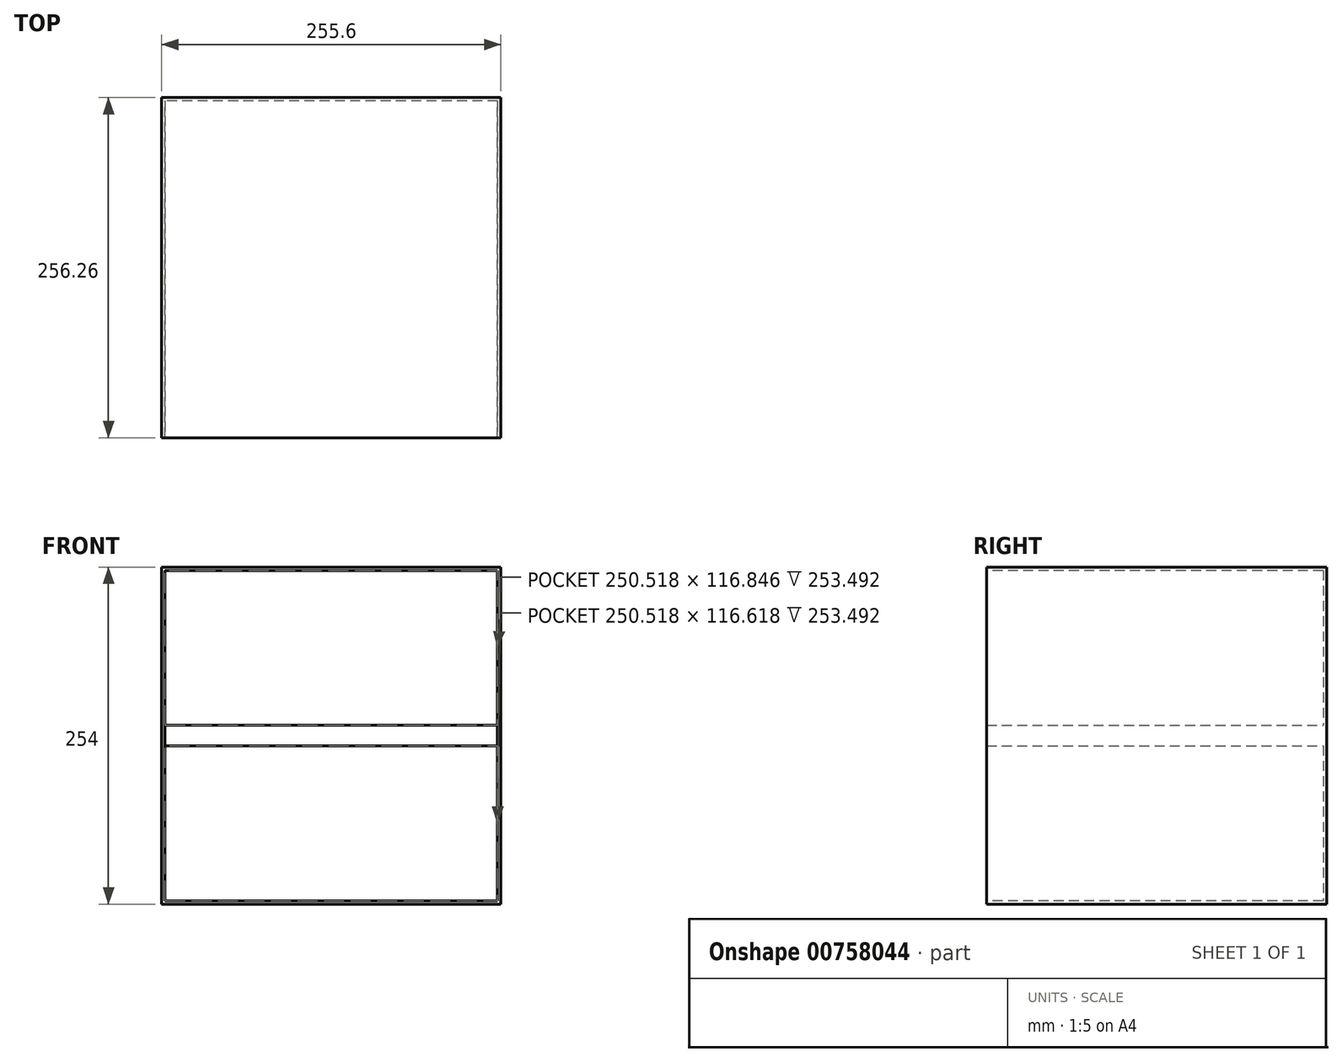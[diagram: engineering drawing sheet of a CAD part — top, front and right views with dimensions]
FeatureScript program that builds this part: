
annotation { "Feature Type Name" : "Feature", "Feature Type Description" : "" }
export const myFeature = defineFeature(function(context is Context, id is Id, definition is map)
    precondition{}
    {
        {
            var Q0;
            Q0=qCreatedBy(makeId("Top.planeOp"),FACE);
            var sketch = newSketch(context, id + "F0", { "sketchPlane" : qUnion([Q0])});
            skLineSegment(sketch, "E0.bottom", {"start": v(-150.52, 117.37) * mm, "end": v(105.08, 117.37) * mm});
            skLineSegment(sketch, "E0.top", {"start": v(-150.52, -138.89) * mm, "end": v(105.08, -138.89) * mm});
            skLineSegment(sketch, "E0.left", {"start": v(-150.52, 117.37) * mm, "end": v(-150.52, -138.89) * mm});
            skLineSegment(sketch, "E0.right", {"start": v(105.08, 117.37) * mm, "end": v(105.08, -138.89) * mm});
            skSolve(sketch);
        }
        {
            var Q0;
            Q0=makeQuery(id+"F0.imprint","IMPRINT",FACE,{"disambiguationData":[TD([[makeQuery(id+"F0.imprint","IMPRINT",EDGE,{"derivedFrom":sQuery(id+"F0.wireOp",EDGE,"E0.bottom")}),-1.0]])]});
            extrude(context, id + "F1", {"entities" : qUnion([Q0]), "depth" : 254 * mm, "offsetDistance" : 25.4 * mm});
        }
        {
            var Q0;
            Q0=makeQuery(id+"F1.opExtrude","SWEPT_FACE",FACE,{"disambiguationData":[OSD([sQuery(id+"F0.wireOp",EDGE,"E0.top")])]});
            shell(context, id + "F2", {"entities" : qUnion([Q0]), "thickness" : 2.54 * mm});
        }
        {
            var Q0;
            Q0=makeQuery(id+"F2.opShell","OFFSET_FACE",FACE,{"disambiguationData":[OSD([sQuery(id+"F0.wireOp",EDGE,"E0.bottom")])]});
            var sketch = newSketch(context, id + "F3", { "sketchPlane" : qUnion([Q0])});
            skLineSegment(sketch, "E1", {"start": v(102.54, 127) * mm, "end": v(102.54, 119.39) * mm});
            skLineSegment(sketch, "E2", {"start": v(102.54, 119.39) * mm, "end": v(-147.98, 119.39) * mm});
            skLineSegment(sketch, "E3", {"start": v(-147.98, 119.39) * mm, "end": v(-147.98, 134.84) * mm});
            skLineSegment(sketch, "E4", {"start": v(-147.98, 134.84) * mm, "end": v(102.54, 134.84) * mm});
            skLineSegment(sketch, "E5", {"start": v(102.54, 134.84) * mm, "end": v(102.54, 119.39) * mm});
            skSolve(sketch);
        }
        {
            var Q0;
            Q0 = qSketchRegion(id + "F3", true);
            var Q1;
            {var subQ0=sQuery(id+"F3.wireOp",EDGE,"E2");Q1=makeQuery(id+"F3.imprint","IMPRINT",FACE,{"disambiguationData":[TD([[makeQuery(id+"F3.imprint","IMPRINT",EDGE,{"derivedFrom":subQ0}),-1.0]])]});}
            extrude(context, id + "F4", {"entities" : qUnion([Q0, Q1]), "operationType" : NewBodyOperationType.ADD, "depth" : 253.5 * mm, "offsetDistance" : 25.4 * mm});
        }
    });
